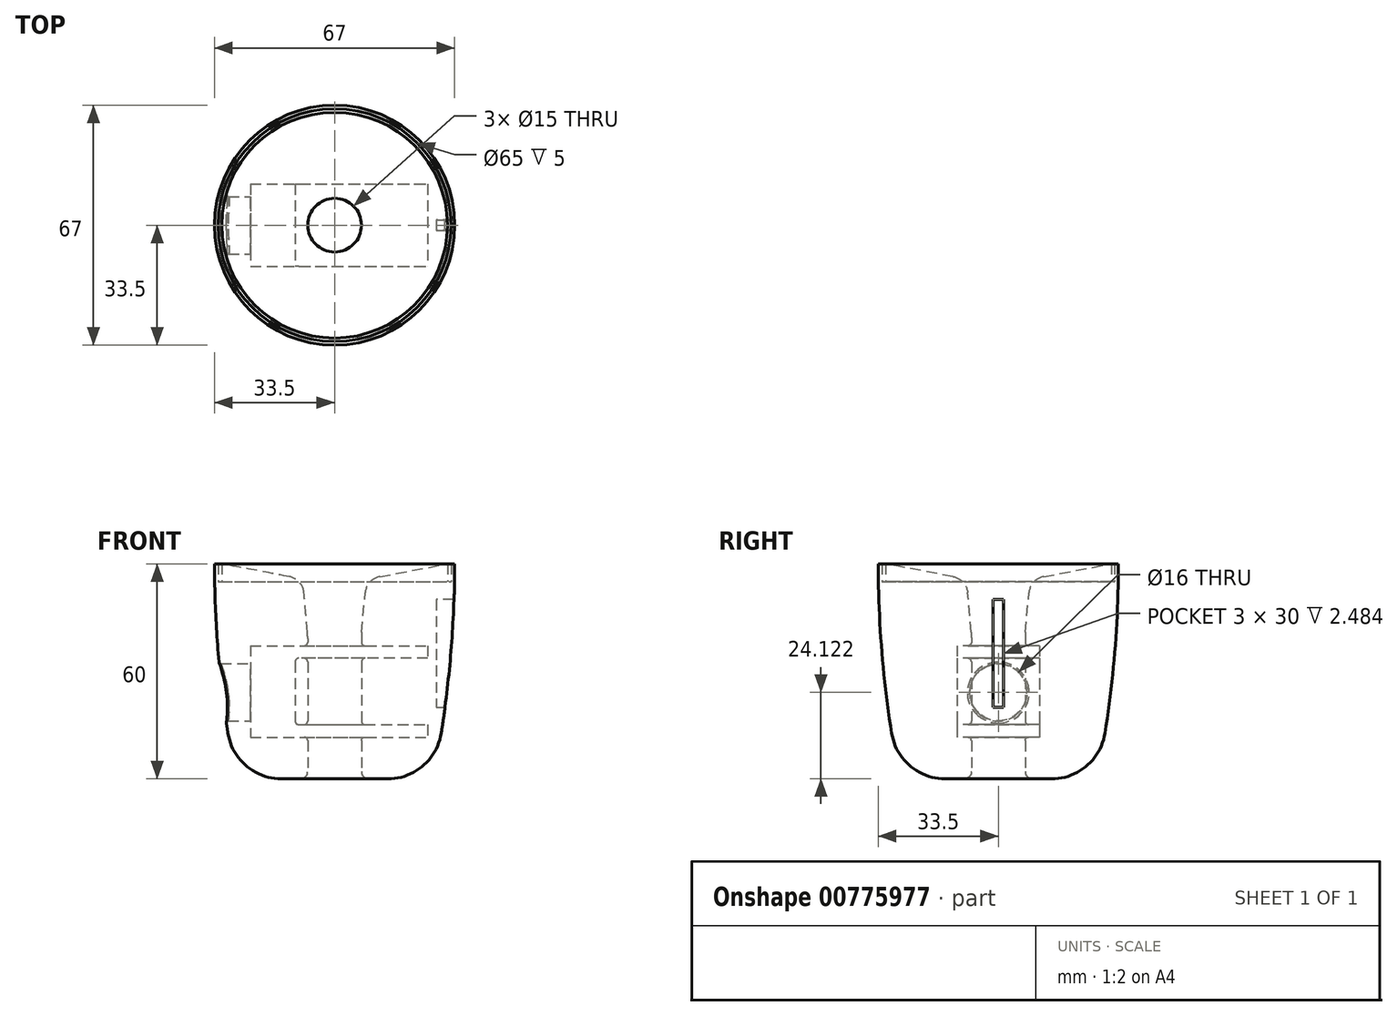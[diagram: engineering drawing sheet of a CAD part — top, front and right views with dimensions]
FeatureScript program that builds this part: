
annotation { "Feature Type Name" : "Feature", "Feature Type Description" : "" }
export const myFeature = defineFeature(function(context is Context, id is Id, definition is map)
    precondition{}
    {
        {
            var Q0;
            Q0=qCreatedBy(makeId("Front.planeOp"),FACE);
            var sketch = newSketch(context, id + "F0", { "sketchPlane" : qUnion([Q0])});
            skLineSegment(sketch, "E0", {"start": v(-33.5, -33.38) * mm, "end": v(-33.5, 26.62) * mm, "construction": true});
            skLineSegment(sketch, "E1", {"start": v(-31.5, 26.62) * mm, "end": v(-12.6, 23.02) * mm});
            skLineSegment(sketch, "E2", {"start": v(-8.54, 18.55) * mm, "end": v(-7.58, 7.49) * mm});
            skLineSegment(sketch, "E3", {"start": v(-7.5, 5.74) * mm, "end": v(-7.5, -33.38) * mm});
            skLineSegment(sketch, "E4", {"start": v(-7.5, -33.38) * mm, "end": v(-33.5, -33.38) * mm, "construction": true});
            skLineSegment(sketch, "E5", {"start": v(0, -36.56) * mm, "end": v(0, 42.73) * mm, "construction": true});
            skArc(sketch, "E6", {"start": v(-33.5, 26.62) * mm, "mid": v(-32.56, 2.88) * mm, "end": v(-29.74, -20.7) * mm});
            skLineSegment(sketch, "E7.bottom", {"start": v(-25.31, 12.07) * mm, "end": v(8.69, 12.07) * mm, "construction": true});
            skLineSegment(sketch, "E7.top", {"start": v(-25.31, -7.93) * mm, "end": v(8.69, -7.93) * mm, "construction": true});
            skLineSegment(sketch, "E7.left", {"start": v(-25.31, 12.07) * mm, "end": v(-25.31, -7.93) * mm, "construction": true});
            skLineSegment(sketch, "E7.right", {"start": v(8.69, 12.07) * mm, "end": v(8.69, -7.93) * mm, "construction": true});
            skLineSegment(sketch, "E8", {"start": v(-33.5, 26.62) * mm, "end": v(-32.5, 26.62) * mm});
            skLineSegment(sketch, "E9", {"start": v(-32.5, 26.62) * mm, "end": v(-32.5, 21.62) * mm});
            skLineSegment(sketch, "E10", {"start": v(-32.5, 21.62) * mm, "end": v(-31.5, 21.62) * mm});
            skLineSegment(sketch, "E11", {"start": v(-31.5, 21.62) * mm, "end": v(-31.5, 26.62) * mm});
            skLineSegment(sketch, "E12", {"start": v(-7.5, -33.38) * mm, "end": v(-7.5, -33.38) * mm});
            skLineSegment(sketch, "E13", {"start": v(-7.5, -33.38) * mm, "end": v(-14.88, -33.38) * mm});
            skPoint(sketch, "E14.visualSharp", {"position": v(-8.87, 22.32) * mm});
            skArc(sketch, "E14.filletArc", {"start": v(-8.54, 18.55) * mm, "mid": v(-9.82, 21.46) * mm, "end": v(-12.6, 23.02) * mm});
            skPoint(sketch, "E15.visualSharp", {"position": v(-7.5, 6.62) * mm});
            skArc(sketch, "E15.filletArc", {"start": v(-7.5, 5.74) * mm, "mid": v(-7.52, 6.62) * mm, "end": v(-7.58, 7.49) * mm});
            skArc(sketch, "E16", {"start": v(-29.74, -20.7) * mm, "mid": v(-24.65, -29.78) * mm, "end": v(-14.88, -33.38) * mm});
            skSolve(sketch);
        }
        {
            var Q0;
            Q0=qSketchRegion(id+"F0",true);
            var Q1;
            Q1=sQuery(id+"F0.wireOp",EDGE,"E5");
            revolve(context, id + "F1", {"surfaceOperationType" : NewSurfaceOperationType.NEW, "entities" : qUnion([Q0]), "axis" : qUnion([Q1]), "revolveType" : RevolveType.FULL});
        }
        {
            var Q0;
            Q0=qCreatedBy(makeId("Front.planeOp"),FACE);
            var sketch = newSketch(context, id + "F2", { "sketchPlane" : qUnion([Q0])});
            skLineSegment(sketch, "E17.bottom", {"start": v(-23.5, 3.74) * mm, "end": v(26, 3.74) * mm});
            skLineSegment(sketch, "E17.top", {"start": v(-23.5, -21.76) * mm, "end": v(26, -21.76) * mm});
            skLineSegment(sketch, "E17.left", {"start": v(-23.5, 3.74) * mm, "end": v(-23.5, -21.76) * mm});
            skLineSegment(sketch, "E17.right", {"start": v(26, 3.74) * mm, "end": v(26, -21.76) * mm, "construction": true});
            skLineSegment(sketch, "E18", {"start": v(26, 3.74) * mm, "end": v(26, 0.24) * mm});
            skLineSegment(sketch, "E19", {"start": v(26, 0.24) * mm, "end": v(-11, 0.24) * mm});
            skLineSegment(sketch, "E20", {"start": v(-11, 0.24) * mm, "end": v(-11, -18.26) * mm});
            skLineSegment(sketch, "E21", {"start": v(-11, -18.26) * mm, "end": v(26, -18.26) * mm});
            skLineSegment(sketch, "E22", {"start": v(26, -18.26) * mm, "end": v(26, -21.76) * mm});
            skSolve(sketch);
        }
        {
            var Q0;
            Q0=qSketchRegion(id+"F2",true);
            extrude(context, id + "F3", {"entities" : qUnion([Q0]), "operationType" : NewBodyOperationType.REMOVE, "endBound" : BoundingType.SYMMETRIC, "oppositeDirection" : true, "depth" : 23 * mm, "offsetDistance" : 25 * mm});
        }
        {
            var Q0;
            Q0=qCreatedBy(makeId("Right.planeOp"),FACE);
            cPlane(context, id + "F4", {"entities" : qUnion([Q0]), "cplaneType" : CPlaneType.OFFSET, "offset" : 18 * mm, "oppositeDirection" : true, "width" : 150 * mm, "height" : 150 * mm});
        }
        {
            var Q0;
            Q0=qCreatedBy(id+"F4.planeOp",FACE);
            var sketch = newSketch(context, id + "F5", { "sketchPlane" : qUnion([Q0])});
            skCircle(sketch, "E23", {"center": v(0, -9.26) * mm, "radius": 8 * mm});
            skSolve(sketch);
        }
        {
            var Q0;
            Q0=qSketchRegion(id+"F5",true);
            extrude(context, id + "F6", {"entities" : qUnion([Q0]), "operationType" : NewBodyOperationType.REMOVE, "oppositeDirection" : true, "depth" : 25 * mm, "offsetDistance" : 25 * mm});
        }
        {
            var Q0;
            Q0=makeQuery(id+"F6.boolean.opBoolean","INTERSECT",EDGE,{"derivedFrom":[makeQuery(id+"F1.opRevolve","SWEPT_FACE",FACE,{"disambiguationData":[OSD([sQuery(id+"F0.wireOp",EDGE,"E6")])]}),makeQuery(id+"F6.opExtrude","SWEPT_FACE",FACE,{"disambiguationData":[OSD([sQuery(id+"F5.wireOp",EDGE,"E23")])]})]});
            fillet(context, id + "F7", {"entities" : qUnion([Q0]), "radius" : 0.5 * mm, "tangentPropagation" : true, "allowEdgeOverflow" : false});
        }
        {
            var Q0;
            Q0=makeQuery(id+"F1.opRevolve","SWEPT_EDGE",EDGE,{"disambiguationData":[OSD([sQuery(id+"F0.wireOp",EDGE,"E12"),sQuery(id+"F0.wireOp",EDGE,"E13")])]});
            fillet(context, id + "F8", {"entities" : qUnion([Q0]), "radius" : 2 * mm, "tangentPropagation" : true, "allowEdgeOverflow" : false});
        }
        {
            var Q0;
            Q0=makeQuery(id+"F3.boolean.opBoolean","INTERSECT",EDGE,{"derivedFrom":[makeQuery(id+"F1.opRevolve","SWEPT_FACE",FACE,{"disambiguationData":[OSD([sQuery(id+"F0.wireOp",EDGE,"E3"),sQuery(id+"F0.wireOp",EDGE,"E12")])]}),makeQuery(id+"F3.opExtrude","SWEPT_FACE",FACE,{"disambiguationData":[OSD([sQuery(id+"F2.wireOp",EDGE,"E17.top")])]})]});
            var Q1;
            Q1=makeQuery(id+"F3.boolean.opBoolean","INTERSECT",EDGE,{"derivedFrom":[makeQuery(id+"F1.opRevolve","SWEPT_FACE",FACE,{"disambiguationData":[OSD([sQuery(id+"F0.wireOp",EDGE,"E3"),sQuery(id+"F0.wireOp",EDGE,"E12")])]}),makeQuery(id+"F3.opExtrude","SWEPT_FACE",FACE,{"disambiguationData":[OSD([sQuery(id+"F2.wireOp",EDGE,"E21")])]})]});
            var Q2;
            Q2=makeQuery(id+"F3.boolean.opBoolean","INTERSECT",EDGE,{"derivedFrom":[makeQuery(id+"F1.opRevolve","SWEPT_FACE",FACE,{"disambiguationData":[OSD([sQuery(id+"F0.wireOp",EDGE,"E3"),sQuery(id+"F0.wireOp",EDGE,"E12")])]}),makeQuery(id+"F3.opExtrude","SWEPT_FACE",FACE,{"disambiguationData":[OSD([sQuery(id+"F2.wireOp",EDGE,"E19")])]})]});
            var Q3;
            Q3=makeQuery(id+"F3.boolean.opBoolean","INTERSECT",EDGE,{"derivedFrom":[makeQuery(id+"F1.opRevolve","SWEPT_FACE",FACE,{"disambiguationData":[OSD([sQuery(id+"F0.wireOp",EDGE,"E3"),sQuery(id+"F0.wireOp",EDGE,"E12")])]}),makeQuery(id+"F3.opExtrude","SWEPT_FACE",FACE,{"disambiguationData":[OSD([sQuery(id+"F2.wireOp",EDGE,"E17.bottom")])]})]});
            var Q4;
            Q4=makeQuery(id+"F3.boolean.opBoolean","COPY",EDGE,{"derivedFrom":makeQuery(id+"F3.opExtrude","SWEPT_EDGE",EDGE,{"disambiguationData":[OSD([sQuery(id+"F2.wireOp",EDGE,"E19"),sQuery(id+"F2.wireOp",EDGE,"E20")])]})});
            var Q5;
            Q5=makeQuery(id+"F3.boolean.opBoolean","COPY",EDGE,{"derivedFrom":makeQuery(id+"F3.opExtrude","SWEPT_EDGE",EDGE,{"disambiguationData":[OSD([sQuery(id+"F2.wireOp",EDGE,"E20"),sQuery(id+"F2.wireOp",EDGE,"E21")])]})});
            fillet(context, id + "F9", {"entities" : qUnion([Q0, Q1, Q2, Q3, Q4, Q5]), "radius" : 1 * mm, "tangentPropagation" : true, "allowEdgeOverflow" : false});
        }
        {
            var Q0;
            Q0=qCreatedBy(makeId("Front.planeOp"),FACE);
            var sketch = newSketch(context, id + "F10", { "sketchPlane" : qUnion([Q0])});
            skLineSegment(sketch, "E24", {"start": v(0.05, 26.62) * mm, "end": v(33.55, 26.62) * mm, "construction": true});
            skLineSegment(sketch, "E25", {"start": v(0.05, 26.62) * mm, "end": v(-33.5, 26.62) * mm, "construction": true});
            skArc(sketch, "E26", {"start": v(-33.5, 26.62) * mm, "mid": v(-32.56, 2.88) * mm, "end": v(-29.74, -20.7) * mm, "construction": true});
            skArc(sketch, "E27.MirrorCS", {"start": v(33.5, 26.62) * mm, "mid": v(32.56, 2.88) * mm, "end": v(29.74, -20.7) * mm, "construction": true});
            skArc(sketch, "E28", {"start": v(30.82, -13.38) * mm, "mid": v(32.45, 1.58) * mm, "end": v(33.33, 16.62) * mm});
            skLineSegment(sketch, "E29", {"start": v(33.33, 16.62) * mm, "end": v(28.33, 16.62) * mm});
            skLineSegment(sketch, "E30", {"start": v(28.33, 16.62) * mm, "end": v(28.33, -13.38) * mm});
            skLineSegment(sketch, "E31", {"start": v(28.33, -13.38) * mm, "end": v(30.82, -13.38) * mm});
            skLineSegment(sketch, "E32", {"start": v(0.05, 26.62) * mm, "end": v(0, 0) * mm, "construction": true});
            skSolve(sketch);
        }
        {
            var Q0;
            Q0=qSketchRegion(id+"F10",true);
            extrude(context, id + "F11", {"entities" : qUnion([Q0]), "operationType" : NewBodyOperationType.REMOVE, "endBound" : BoundingType.SYMMETRIC, "oppositeDirection" : true, "depth" : 3 * mm, "offsetDistance" : 25 * mm});
        }
        {
            var Q0;
            Q0=makeQuery(id+"F3.boolean.opBoolean","COPY",VERTEX,{"derivedFrom":makeQuery(id+"F3.opExtrude","CAP_VERTEX",VERTEX,{"disambiguationData":[OSD([sQuery(id+"F2.wireOp",EDGE,"E17.bottom"),sQuery(id+"F2.wireOp",EDGE,"E17.left")])],"isStart":false})});
            var Q1;
            Q1=makeQuery(id+"F3.boolean.opBoolean","COPY",VERTEX,{"derivedFrom":makeQuery(id+"F3.opExtrude","CAP_VERTEX",VERTEX,{"disambiguationData":[OSD([sQuery(id+"F2.wireOp",EDGE,"E17.bottom"),sQuery(id+"F2.wireOp",EDGE,"E17.left")])],"isStart":true})});
            var Q2;
            Q2=makeQuery(id+"F3.boolean.opBoolean","COPY",VERTEX,{"derivedFrom":makeQuery(id+"F3.opExtrude","CAP_VERTEX",VERTEX,{"disambiguationData":[OSD([sQuery(id+"F2.wireOp",EDGE,"E17.bottom"),sQuery(id+"F2.wireOp",EDGE,"E18")])],"isStart":true})});
            cPlane(context, id + "F12", {"entities" : qUnion([Q0, Q1, Q2]), "cplaneType" : CPlaneType.THREE_POINT, "offset" : 25 * mm, "width" : 150 * mm, "height" : 150 * mm});
        }
    });
